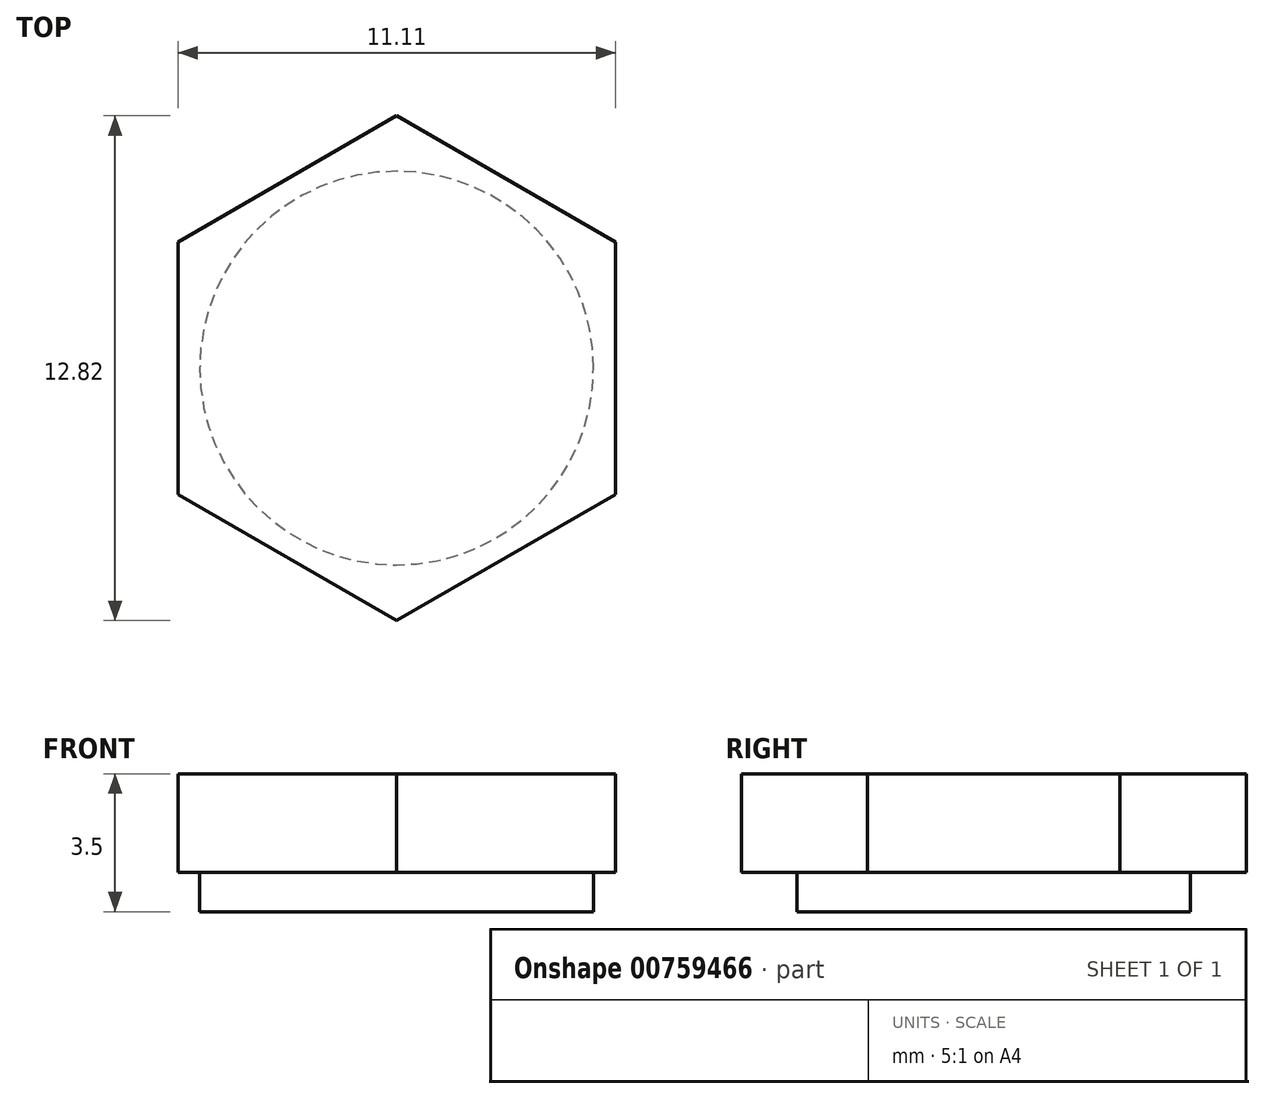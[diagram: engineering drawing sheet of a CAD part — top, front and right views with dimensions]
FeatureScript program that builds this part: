
annotation { "Feature Type Name" : "Feature", "Feature Type Description" : "" }
export const myFeature = defineFeature(function(context is Context, id is Id, definition is map)
    precondition{}
    {
        {
            var Q0;
            Q0=qCreatedBy(makeId("Top.planeOp"),FACE);
            var sketch = newSketch(context, id + "F0", { "sketchPlane" : qUnion([Q0])});
            skCircle(sketch, "E0.cCircle", {"center": v(0, 0) * mm, "radius": 5.55 * mm, "construction": true});
            skLineSegment(sketch, "E0.0", {"start": v(5.55, 3.2) * mm, "end": v(5.55, -3.2) * mm});
            skLineSegment(sketch, "E0.1", {"start": v(5.56, -3.2) * mm, "end": v(0, -6.41) * mm});
            skLineSegment(sketch, "E0.2", {"start": v(0, -6.41) * mm, "end": v(-5.56, -3.2) * mm});
            skLineSegment(sketch, "E0.3", {"start": v(-5.55, -3.2) * mm, "end": v(-5.56, 3.2) * mm});
            skLineSegment(sketch, "E0.4", {"start": v(-5.56, 3.2) * mm, "end": v(0, 6.41) * mm});
            skLineSegment(sketch, "E0.5", {"start": v(0, 6.41) * mm, "end": v(5.56, 3.2) * mm});
            skPoint(sketch, "E0.0.midPoint", {"position": v(5.55, 0) * mm});
            skCircle(sketch, "E1", {"center": v(0, 0) * mm, "radius": 5 * mm});
            skSolve(sketch);
        }
        {
            var Q0;
            Q0 = qSketchRegion(id + "F0", true);
            var Q1;
            Q1=makeQuery(id+"F0.imprint","IMPRINT",FACE,{"disambiguationData":[TD([[makeQuery(id+"F0.imprint","IMPRINT",EDGE,{"derivedFrom":sQuery(id+"F0.wireOp",EDGE,"E1")}),1.0]])]});
            extrude(context, id + "F1", {"entities" : qUnion([Q0, Q1]), "depth" : 2.5 * mm, "offsetDistance" : 25 * mm});
        }
        {
            var Q0;
            Q0=makeQuery(id+"F0.imprint","IMPRINT",FACE,{"disambiguationData":[TD([[makeQuery(id+"F0.imprint","IMPRINT",EDGE,{"derivedFrom":sQuery(id+"F0.wireOp",EDGE,"E1")}),1.0]])]});
            extrude(context, id + "F2", {"entities" : qUnion([Q0]), "operationType" : NewBodyOperationType.ADD, "oppositeDirection" : true, "depth" : 1 * mm, "offsetDistance" : 25 * mm});
        }
    });
